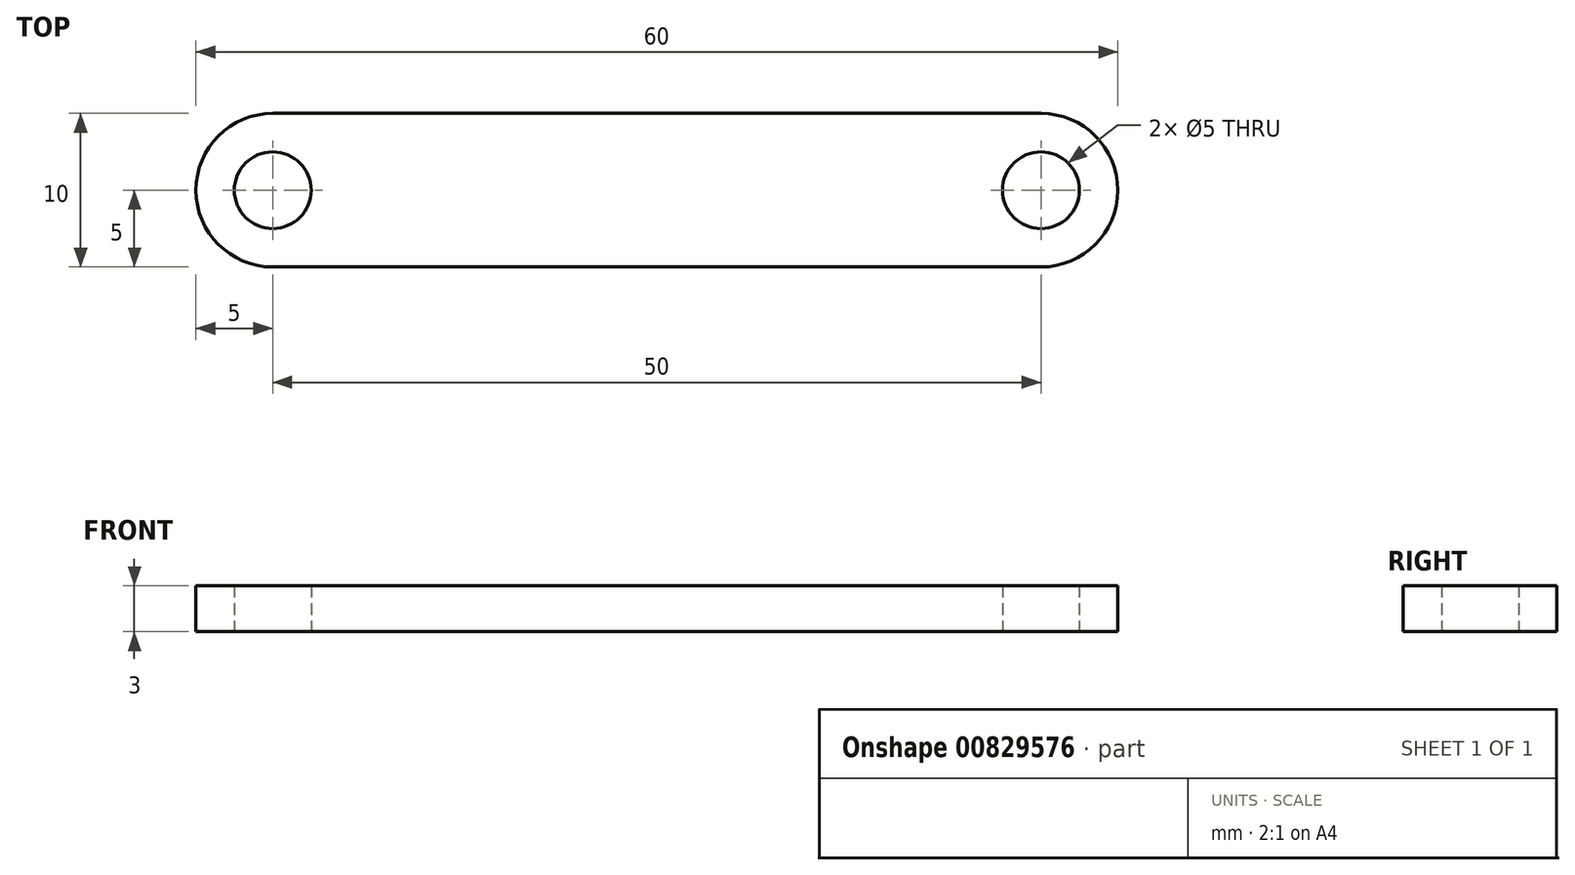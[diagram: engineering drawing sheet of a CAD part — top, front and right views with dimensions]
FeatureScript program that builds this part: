
annotation { "Feature Type Name" : "Feature", "Feature Type Description" : "" }
export const myFeature = defineFeature(function(context is Context, id is Id, definition is map)
    precondition{}
    {
        {
            var Q0;
            Q0=qCreatedBy(makeId("Top.planeOp"),FACE);
            var sketch = newSketch(context, id + "F0", { "sketchPlane" : qUnion([Q0])});
            skArc(sketch, "E0", {"start": v(0, 5) * mm, "mid": v(-5, 0) * mm, "end": v(0, -5) * mm});
            skArc(sketch, "E1", {"start": v(50, -5) * mm, "mid": v(55, 0) * mm, "end": v(50, 5) * mm});
            skLineSegment(sketch, "E2", {"start": v(0, 5) * mm, "end": v(50, 5) * mm});
            skLineSegment(sketch, "E3", {"start": v(0, -5) * mm, "end": v(50, -5) * mm});
            skCircle(sketch, "E4", {"center": v(0, 0) * mm, "radius": 2.5 * mm});
            skCircle(sketch, "E5", {"center": v(50, 0) * mm, "radius": 2.5 * mm});
            skSolve(sketch);
        }
        {
            var Q0;
            Q0=makeQuery(id+"F0.imprint","IMPRINT",FACE,{"disambiguationData":[TD([[makeQuery(id+"F0.imprint","IMPRINT",EDGE,{"derivedFrom":sQuery(id+"F0.wireOp",EDGE,"E0")}),1.0]])]});
            extrude(context, id + "F1", {"entities" : qUnion([Q0]), "depth" : 3 * mm, "offsetDistance" : 25 * mm});
        }
    });
